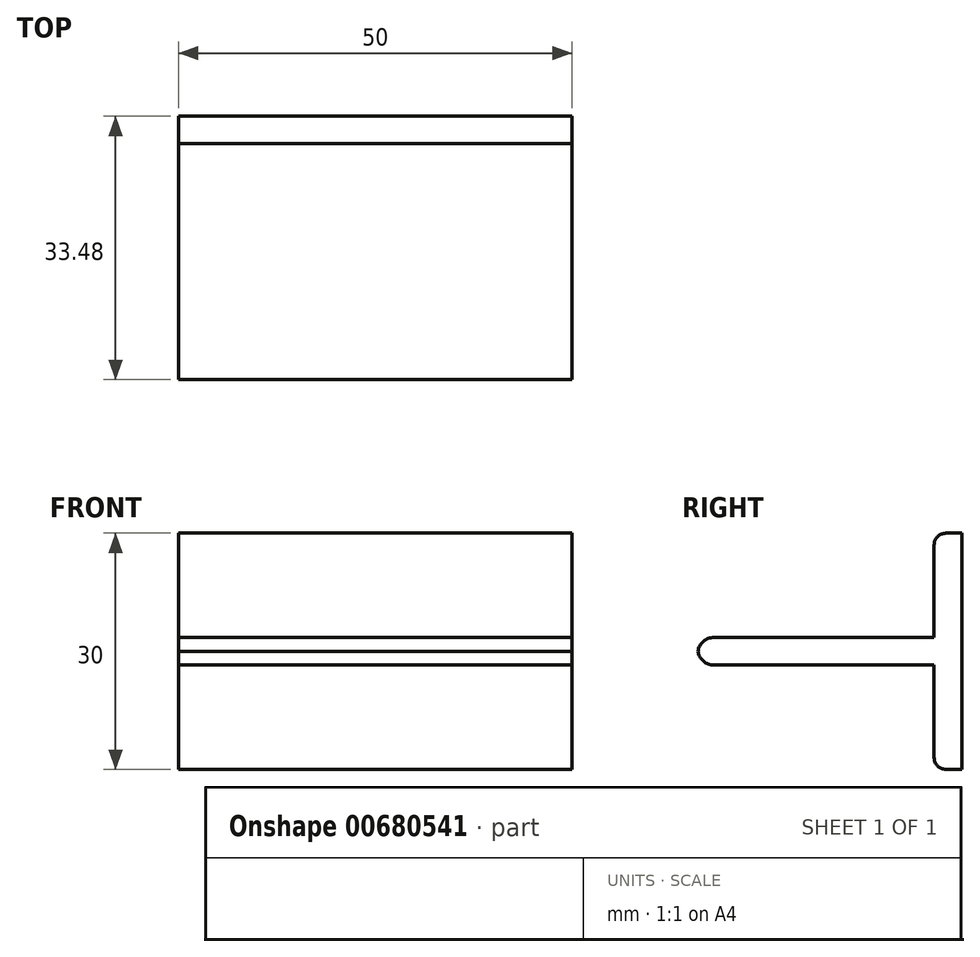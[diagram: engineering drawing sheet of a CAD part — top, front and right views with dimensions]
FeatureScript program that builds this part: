
annotation { "Feature Type Name" : "Feature", "Feature Type Description" : "" }
export const myFeature = defineFeature(function(context is Context, id is Id, definition is map)
    precondition{}
    {
        {
            var Q0;
            Q0=qCreatedBy(makeId("Front.planeOp"),FACE);
            var sketch = newSketch(context, id + "F0", { "sketchPlane" : qUnion([Q0])});
            skLineSegment(sketch, "E0.bottom", {"start": v(25, 15) * mm, "end": v(-25, 15) * mm});
            skLineSegment(sketch, "E0.top", {"start": v(25, -15) * mm, "end": v(-25, -15) * mm});
            skLineSegment(sketch, "E0.left", {"start": v(25, 15) * mm, "end": v(25, -15) * mm});
            skLineSegment(sketch, "E0.right", {"start": v(-25, 15) * mm, "end": v(-25, -15) * mm});
            skPoint(sketch, "E0.middle", {"position": v(0, 0) * mm});
            skSolve(sketch);
        }
        {
            var Q0;
            Q0 = qSketchRegion(id + "F0", true);
            extrude(context, id + "F1", {"entities" : qUnion([Q0]), "depth" : 3.5 * mm, "offsetDistance" : 25 * mm});
        }
        {
            var Q0;
            Q0=makeQuery(id+"F1.opExtrude","CAP_EDGE",EDGE,{"disambiguationData":[OSD([sQuery(id+"F0.wireOp",EDGE,"E0.bottom")])],"isStart":false});
            var Q1;
            Q1=makeQuery(id+"F1.opExtrude","CAP_EDGE",EDGE,{"disambiguationData":[OSD([sQuery(id+"F0.wireOp",EDGE,"E0.top")])],"isStart":false});
            fillet(context, id + "F2", {"entities" : qUnion([Q0, Q1]), "radius" : 1.5 * mm, "tangentPropagation" : true, "allowEdgeOverflow" : false});
        }
        {
            var Q0;
            Q0=makeQuery(id+"F1.opExtrude","CAP_FACE",FACE,{"disambiguationData":[OSD([sQuery(id+"F0.wireOp",EDGE,"E0.bottom"),sQuery(id+"F0.wireOp",EDGE,"E0.top"),sQuery(id+"F0.wireOp",EDGE,"E0.left"),sQuery(id+"F0.wireOp",EDGE,"E0.right")])],"isStart":false});
            var sketch = newSketch(context, id + "F3", { "sketchPlane" : qUnion([Q0])});
            skLineSegment(sketch, "E1", {"start": v(-25, 1.75) * mm, "end": v(25, 1.75) * mm});
            skLineSegment(sketch, "E2", {"start": v(25, 1.75) * mm, "end": v(25, -1.75) * mm});
            skLineSegment(sketch, "E3", {"start": v(25, -1.75) * mm, "end": v(-25, -1.75) * mm});
            skLineSegment(sketch, "E4", {"start": v(-25, -1.75) * mm, "end": v(-25, 1.75) * mm});
            skSolve(sketch);
        }
        {
            var Q0;
            Q0=makeQuery(id+"F3.imprint","IMPRINT",FACE,{"disambiguationData":[TD([[makeQuery(id+"F3.imprint","IMPRINT",EDGE,{"derivedFrom":sQuery(id+"F3.wireOp",EDGE,"E1")}),-1.0]])]});
            extrude(context, id + "F4", {"entities" : qUnion([Q0]), "operationType" : NewBodyOperationType.ADD, "depth" : 30 * mm, "offsetDistance" : 25 * mm});
        }
        {
            var Q0;
            Q0=makeQuery(id+"F4.opExtrude","CAP_EDGE",EDGE,{"disambiguationData":[OSD([sQuery(id+"F3.wireOp",EDGE,"E3")])],"isStart":false});
            var Q1;
            Q1=makeQuery(id+"F4.opExtrude","CAP_EDGE",EDGE,{"disambiguationData":[OSD([sQuery(id+"F3.wireOp",EDGE,"E1")])],"isStart":false});
            fillet(context, id + "F5", {"entities" : qUnion([Q0, Q1]), "radius" : 2 * mm, "tangentPropagation" : true, "allowEdgeOverflow" : false});
        }
    });
